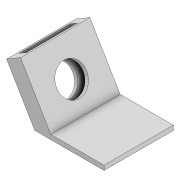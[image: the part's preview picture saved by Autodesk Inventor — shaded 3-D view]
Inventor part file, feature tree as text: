
AUTODESK INVENTOR PART (.ipt)
format: ipt  version: 2022 (Build 260153000, 153)  size: 119,296 bytes
history: native  units: mm
features: extrude x3, sketch x3
ambient origin geometry x8: Origin, YZ Plane, XZ Plane, XY Plane, X Axis, Y Axis, Z Axis, Center Point
bodies: Solid1 (feature_tree)
feature tree (6):
  extrude  "Extrusion1"  Depth=24.0mm
  extrude  "Extrusion2"  Depth=7.0mm
  extrude  "Extrusion3"  Depth=30.0mm TaperAngle=0.0deg
  sketch  "Sketch1"  dims[d0=30.0mm d1=24.0mm]
  sketch  "Sketch2"  dims[d2=21.031217mm d3=7.0mm]
  sketch  "Sketch3"  dims[d4=2.0mm d5=30.0mm d6=0.0mm d7=22.0mm d8=3.5mm d9=7.0mm d10=30.0mm d11=4.0mm d12=1.75mm d13=0.0mm d14=0.0mm d15=13.0mm d16=30.0mm d17=15.0mm d18=14.0mm d19=0.0mm d20=0.0mm]
